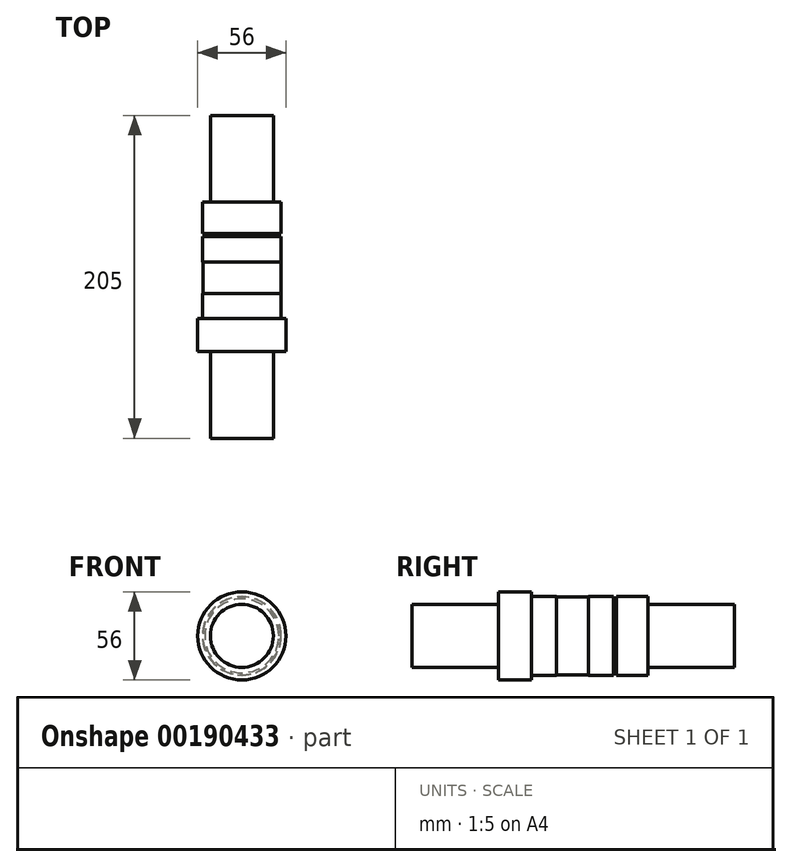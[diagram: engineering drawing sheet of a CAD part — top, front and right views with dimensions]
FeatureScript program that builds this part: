
annotation { "Feature Type Name" : "Feature", "Feature Type Description" : "" }
export const myFeature = defineFeature(function(context is Context, id is Id, definition is map)
    precondition{}
    {
        {
            var Q0;
            Q0=qCreatedBy(makeId("Front.planeOp"),FACE);
            var sketch = newSketch(context, id + "F0", { "sketchPlane" : qUnion([Q0])});
            skCircle(sketch, "E0", {"center": v(0, 0) * mm, "radius": 24.75 * mm});
            skSolve(sketch);
        }
        {
            var Q0;
            Q0=makeQuery(id+"F0.imprint","IMPRINT",FACE,{"disambiguationData":[TD([[makeQuery(id+"F0.imprint","IMPRINT",EDGE,{"derivedFrom":sQuery(id+"F0.wireOp",EDGE,"E0")}),1.0]])]});
            extrude(context, id + "F1", {"entities" : qUnion([Q0]), "depth" : 20 * mm});
        }
        {
            var Q0;
            Q0=makeQuery(id+"F1.opExtrude","CAP_FACE",FACE,{"disambiguationData":[OSD([sQuery(id+"F0.wireOp",EDGE,"E0")])],"isStart":false});
            var sketch = newSketch(context, id + "F2", { "sketchPlane" : qUnion([Q0])});
            skCircle(sketch, "E1", {"center": v(0, 0) * mm, "radius": 25 * mm});
            skSolve(sketch);
        }
        {
            var Q0;
            Q0 = qSketchRegion(id + "F2", true);
            extrude(context, id + "F3", {"entities" : qUnion([Q0]), "operationType" : NewBodyOperationType.ADD, "depth" : 16 * mm});
        }
        {
            var Q0;
            Q0=makeQuery(id+"F1.opExtrude","CAP_FACE",FACE,{"disambiguationData":[OSD([sQuery(id+"F0.wireOp",EDGE,"E0")])],"isStart":true});
            var sketch = newSketch(context, id + "F4", { "sketchPlane" : qUnion([Q0])});
            skCircle(sketch, "E2", {"center": v(0, 0) * mm, "radius": 25 * mm});
            skSolve(sketch);
        }
        {
            var Q0;
            Q0 = qSketchRegion(id + "F4", true);
            extrude(context, id + "F5", {"entities" : qUnion([Q0]), "operationType" : NewBodyOperationType.ADD, "depth" : 16 * mm});
        }
        {
            var Q0;
            Q0=makeQuery(id+"F3.opExtrude","CAP_FACE",FACE,{"disambiguationData":[OSD([sQuery(id+"F2.wireOp",EDGE,"E1")])],"isStart":false});
            var sketch = newSketch(context, id + "F6", { "sketchPlane" : qUnion([Q0])});
            skCircle(sketch, "E3", {"center": v(0, 0) * mm, "radius": 28 * mm});
            skSolve(sketch);
        }
        {
            var Q0;
            Q0 = qSketchRegion(id + "F6", true);
            extrude(context, id + "F7", {"entities" : qUnion([Q0]), "operationType" : NewBodyOperationType.ADD, "depth" : 21 * mm});
        }
        {
            var Q0;
            Q0=makeQuery(id+"F7.opExtrude","CAP_FACE",FACE,{"disambiguationData":[OSD([sQuery(id+"F6.wireOp",EDGE,"E3")])],"isStart":false});
            var sketch = newSketch(context, id + "F8", { "sketchPlane" : qUnion([Q0])});
            skCircle(sketch, "E4", {"center": v(0, 0) * mm, "radius": 20 * mm});
            skSolve(sketch);
        }
        {
            var Q0;
            Q0 = qSketchRegion(id + "F8", true);
            extrude(context, id + "F9", {"entities" : qUnion([Q0]), "operationType" : NewBodyOperationType.ADD, "depth" : 55 * mm});
        }
        {
            var Q0;
            Q0=makeQuery(id+"F5.opExtrude","CAP_FACE",FACE,{"disambiguationData":[OSD([sQuery(id+"F4.wireOp",EDGE,"E2")])],"isStart":false});
            var sketch = newSketch(context, id + "F10", { "sketchPlane" : qUnion([Q0])});
            skCircle(sketch, "E5", {"center": v(0, 0) * mm, "radius": 23.5 * mm});
            skSolve(sketch);
        }
        {
            var Q0;
            Q0 = qSketchRegion(id + "F10", true);
            extrude(context, id + "F11", {"entities" : qUnion([Q0]), "operationType" : NewBodyOperationType.ADD, "depth" : 2 * mm});
        }
        {
            var Q0;
            Q0=makeQuery(id+"F11.opExtrude","CAP_FACE",FACE,{"disambiguationData":[OSD([sQuery(id+"F10.wireOp",EDGE,"E5")])],"isStart":false});
            var sketch = newSketch(context, id + "F12", { "sketchPlane" : qUnion([Q0])});
            skCircle(sketch, "E6", {"center": v(0, 0) * mm, "radius": 25 * mm});
            skSolve(sketch);
        }
        {
            var Q0;
            Q0 = qSketchRegion(id + "F12", true);
            extrude(context, id + "F13", {"entities" : qUnion([Q0]), "operationType" : NewBodyOperationType.ADD, "depth" : 20 * mm});
        }
        {
            var Q0;
            Q0=makeQuery(id+"F13.opExtrude","CAP_FACE",FACE,{"disambiguationData":[OSD([sQuery(id+"F12.wireOp",EDGE,"E6")])],"isStart":false});
            var sketch = newSketch(context, id + "F14", { "sketchPlane" : qUnion([Q0])});
            skCircle(sketch, "E7", {"center": v(0, 0) * mm, "radius": 20 * mm});
            skSolve(sketch);
        }
        {
            var Q0;
            Q0 = qSketchRegion(id + "F14", true);
            extrude(context, id + "F15", {"entities" : qUnion([Q0]), "operationType" : NewBodyOperationType.ADD, "depth" : 55 * mm});
        }
    });
